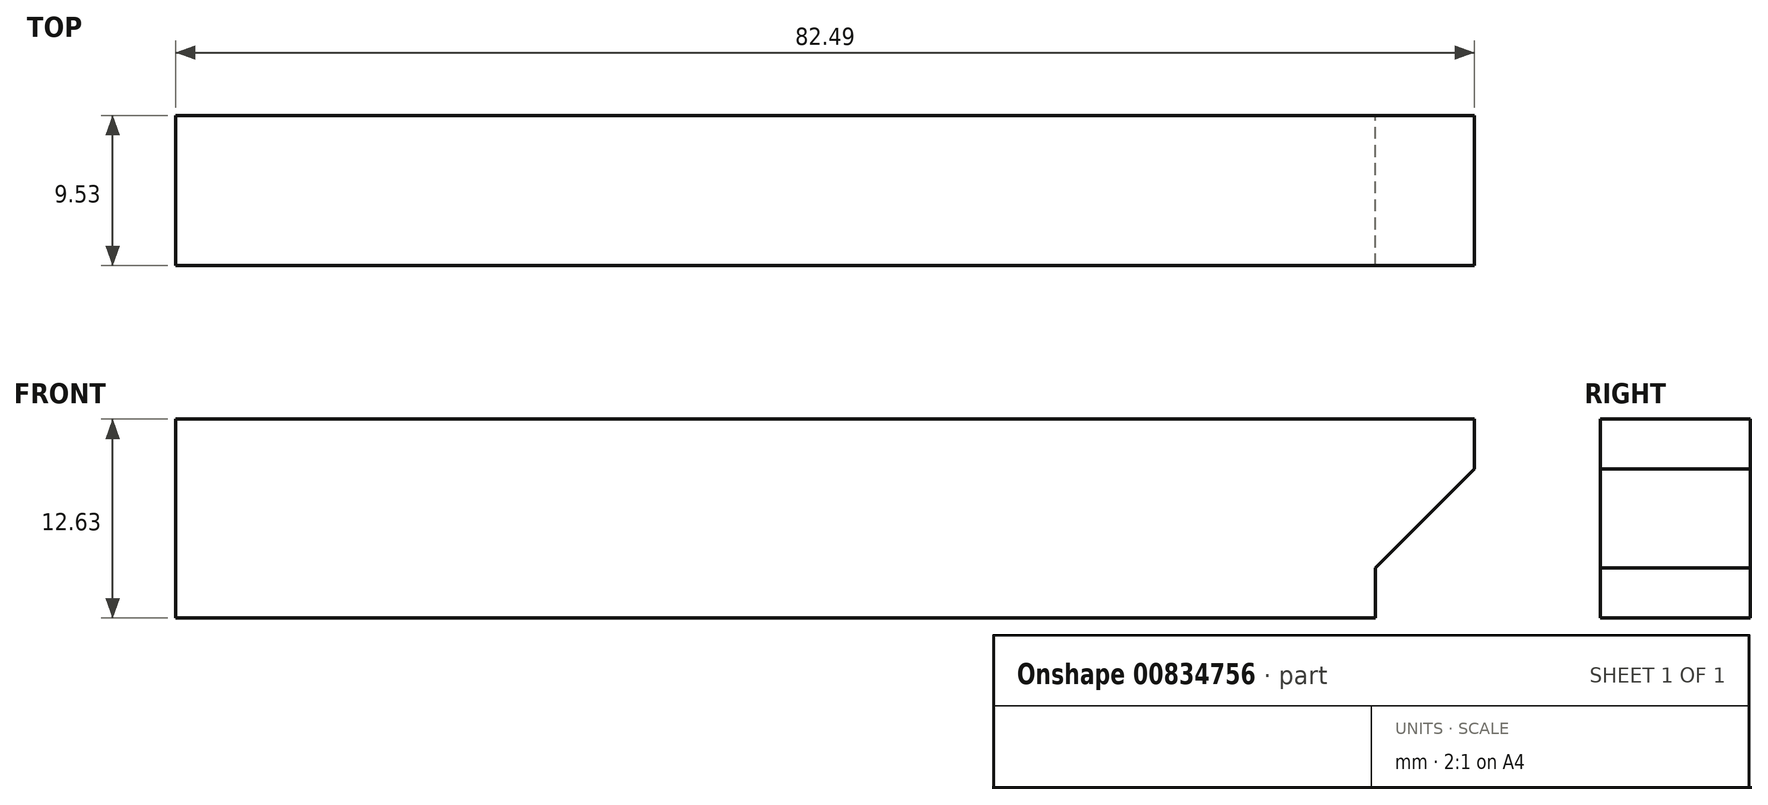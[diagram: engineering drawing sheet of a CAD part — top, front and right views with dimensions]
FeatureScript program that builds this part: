
annotation { "Feature Type Name" : "Feature", "Feature Type Description" : "" }
export const myFeature = defineFeature(function(context is Context, id is Id, definition is map)
    precondition{}
    {
        {
            var Q0;
            Q0=qCreatedBy(makeId("Front.planeOp"),FACE);
            var sketch = newSketch(context, id + "F0", { "sketchPlane" : qUnion([Q0])});
            skLineSegment(sketch, "E0", {"start": v(0, 0) * mm, "end": v(6.29, 6.29) * mm});
            skLineSegment(sketch, "E1", {"start": v(6.29, 6.29) * mm, "end": v(-13.88, 6.29) * mm, "construction": true});
            skLineSegment(sketch, "E2", {"start": v(0, 0) * mm, "end": v(4.32, 0) * mm, "construction": true});
            skLineSegment(sketch, "E3", {"start": v(0, 0) * mm, "end": v(0, 6.29) * mm, "construction": true});
            skLineSegment(sketch, "E4", {"start": v(6.29, 6.29) * mm, "end": v(6.29, 9.46) * mm});
            skLineSegment(sketch, "E5", {"start": v(6.29, 9.46) * mm, "end": v(-76.2, 9.46) * mm});
            skLineSegment(sketch, "E6", {"start": v(-76.2, -3.18) * mm, "end": v(-76.2, 9.46) * mm});
            skLineSegment(sketch, "E7", {"start": v(0, 0) * mm, "end": v(0, -3.18) * mm});
            skLineSegment(sketch, "E8", {"start": v(0, -3.18) * mm, "end": v(-76.2, -3.18) * mm});
            skSolve(sketch);
        }
        {
            var Q0;
            Q0 = qSketchRegion(id + "F0", true);
            extrude(context, id + "F1", {"entities" : qUnion([Q0]), "depth" : 9.52 * mm, "offsetDistance" : 25.4 * mm});
        }
    });
